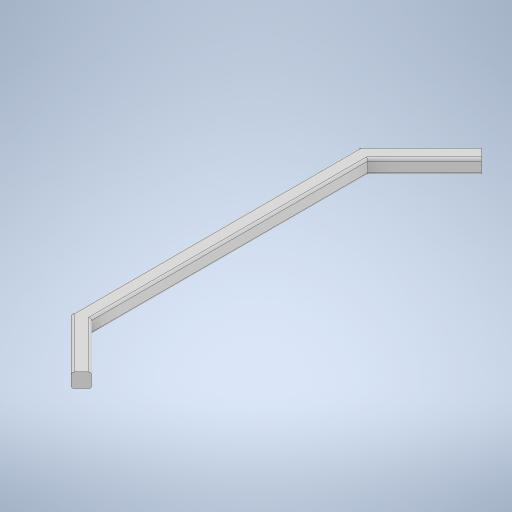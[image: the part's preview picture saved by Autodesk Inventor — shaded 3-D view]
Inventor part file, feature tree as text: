
AUTODESK INVENTOR PART (.ipt)
format: ipt  version: 2023 (Build 270158000, 158)  size: 515,584 bytes
history: native  units: mm
features: other x2, extrude x1, fillet x1, sketch x1
ambient origin geometry x8: Origin, YZ Plane, XZ Plane, XY Plane, X Axis, Y Axis, Z Axis, Center Point
bodies: Body1 (feature_tree)
feature tree (5):
  extrude  "Extrusion2"  Depth=20.0mm
  fillet  "Fillet1"  [1 undecoded]
  sketch  "Sketch1"  dims[d55=135.0deg d56=20.0mm d60=90.0deg d61=100.0mm d62=20.0mm d63=90.0deg d64=80.0mm d80=20.0mm d81=0.0mm d84=3.0mm d22=0.5mm d23=0.872665mm d24=0.5mm d25=0.872665mm]
  other  "Image2"
  other  "Image3"
note: 1 required parameter value undecoded (feature->parameter linkage not recoverable at this tier; creation-order binding heuristic only, values carry confidence <= 0.55)
